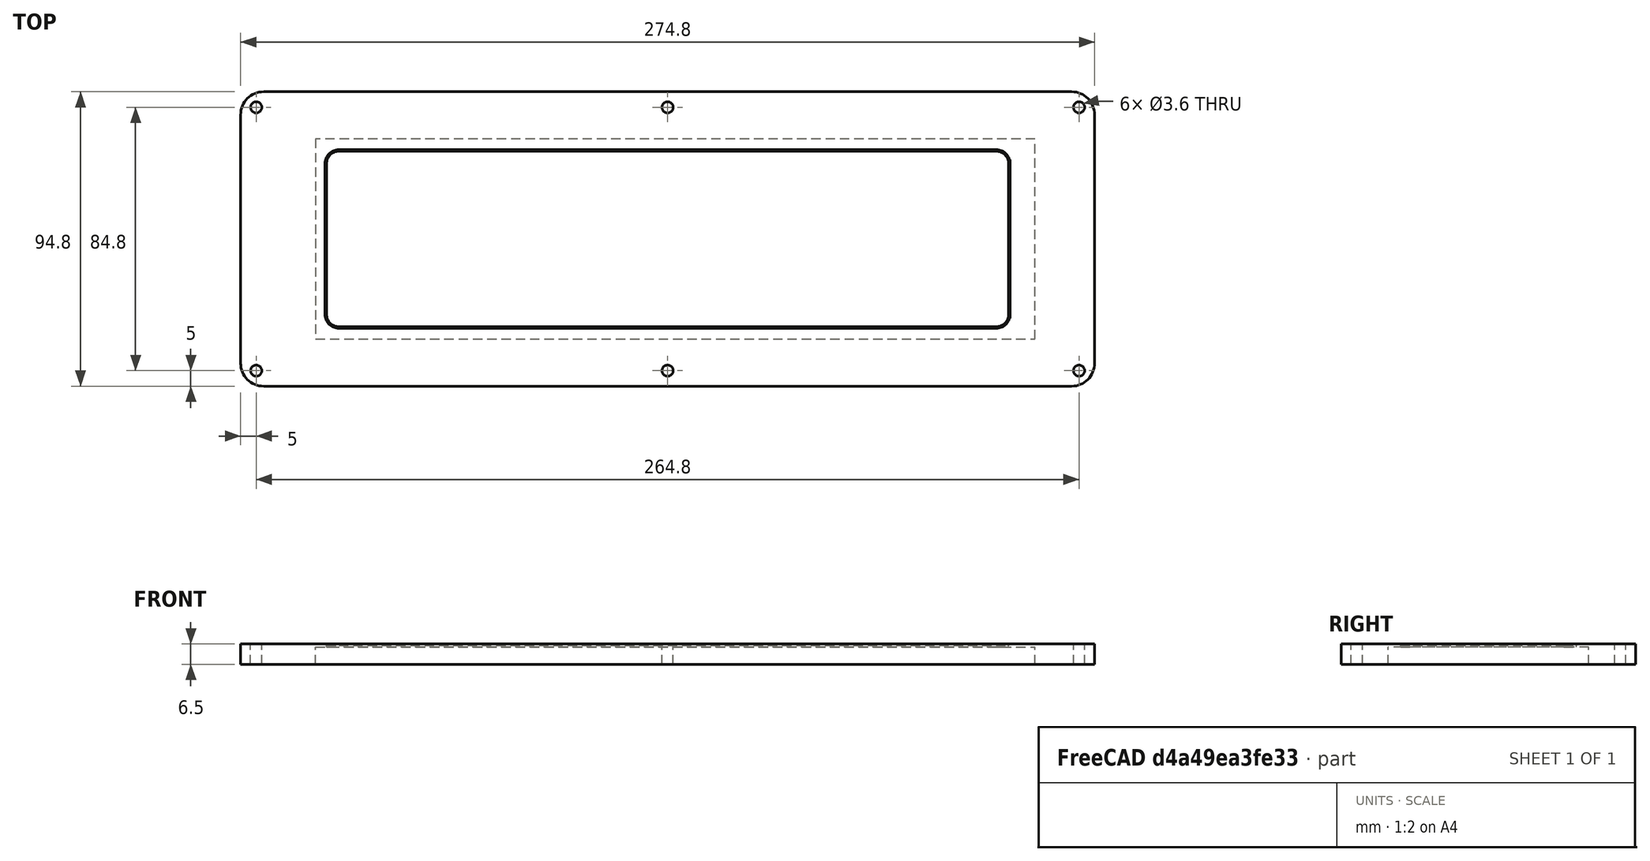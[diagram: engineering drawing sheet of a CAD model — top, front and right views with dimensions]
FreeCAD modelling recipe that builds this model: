
FCSTD DOCUMENT  (FreeCAD 1.0R39319 (Git))
Label: TopEnclosureDisplayFront
License: All rights reserved
LicenseURL: https://en.wikipedia.org/wiki/All_rights_reserved
objects: PartDesign::SubShapeBinder×5, PartDesign::Mirrored×3, App::Link×2, PartDesign::Pocket×2, PartDesign::Hole×2, PartDesign::Pad×1, PartDesign::MultiTransform×1, PartDesign::Chamfer×1, PartDesign::Body×1
note: 32 computed .brp shape members not serialized (recipe doc carries the construction recipe); baked Part::Feature solids carry a one-line shape summary decoded from their .brp
EXTERNAL_REF file=TopEnclosure.FCStd obj=Sketch
EXTERNAL_REF file=Spec.FCStd obj=Spreadsheet

FEATURE [App::Link] Link  label="MasterSketch"
  LinkedObject = -> <external TopEnclosure.FCStd>#Sketch
FEATURE [PartDesign::SubShapeBinder] Binder
  BindCopyOnChange = 0
  BindMode = 0
  ClaimChildren = false
  Context = -> Body [Binder.]
  Fuse = false
  MakeFace = true
  OffsetFill = false
  OffsetIntersection = false
  OffsetJoinType = 0
  OffsetOpenResult = false
  PartialLoad = false
  Refine = true
  Relative = true
  Support = -> [Link[Edge10,Edge9,Edge11,Edge12,Edge13,Edge14,Edge15,Edge16]]
  _Version = 2
FEATURE [PartDesign::SubShapeBinder] Binder001
  BindCopyOnChange = 0
  BindMode = 0
  ClaimChildren = false
  Context = -> Body [Binder001.]
  Fuse = false
  MakeFace = true
  OffsetFill = false
  OffsetIntersection = false
  OffsetJoinType = 0
  OffsetOpenResult = false
  PartialLoad = false
  Refine = true
  Relative = true
  Support = -> [Link[Edge39]]
  _Version = 2
FEATURE [PartDesign::SubShapeBinder] Binder002
  BindCopyOnChange = 0
  BindMode = 0
  ClaimChildren = false
  Context = -> Body [Binder002.]
  Fuse = false
  MakeFace = true
  OffsetFill = false
  OffsetIntersection = false
  OffsetJoinType = 0
  OffsetOpenResult = false
  PartialLoad = false
  Refine = true
  Relative = true
  Support = -> [Link[Edge40]]
  _Version = 2
FEATURE [PartDesign::SubShapeBinder] Binder004
  BindCopyOnChange = 0
  BindMode = 0
  ClaimChildren = false
  Context = -> Body [Binder004.]
  Fuse = false
  MakeFace = true
  OffsetFill = false
  OffsetIntersection = false
  OffsetJoinType = 0
  OffsetOpenResult = false
  PartialLoad = false
  Refine = true
  Relative = true
  Support = -> [Link[Edge35,Edge36,Edge33,Edge34]]
  _Version = 2
FEATURE [PartDesign::SubShapeBinder] Binder005
  BindCopyOnChange = 0
  BindMode = 0
  ClaimChildren = false
  Context = -> Body [Binder005.]
  Fuse = false
  MakeFace = true
  OffsetFill = false
  OffsetIntersection = false
  OffsetJoinType = 0
  OffsetOpenResult = false
  PartialLoad = false
  Refine = true
  Relative = true
  Support = -> [Link[Edge26,Edge25,Edge27,Edge32,Edge31,Edge28,Edge29,Edge30]]
  _Version = 2
FEATURE [App::Link] Link001  label="Vars"
  LinkedObject = -> <external Spec.FCStd>#Spreadsheet
FEATURE [PartDesign::Pad] Pad
  Direction = (0,0,1)
  Length = 6.5
  Length2 = 10
  Profile = -> Binder
  Refine = true
  Suppressed = false
  Type = 0
  expr: Length = <<Vars>>.display_depth + <<Vars>>.top_enclosure_front_depth
FEATURE [PartDesign::Pocket] Pocket
  BaseFeature = -> Pad
  Direction = (0,0,-1)
  Length = 5
  Length2 = 5
  Profile = -> Binder005
  Refine = true
  Reversed = true
  Suppressed = false
  Type = 1
FEATURE [PartDesign::Pocket] Pocket001
  BaseFeature = -> Pocket
  Direction = (0,0,-1)
  Length = 5.5
  Length2 = 5
  Profile = -> Binder004
  Refine = true
  Reversed = true
  Suppressed = false
  Type = 0
  expr: Length = <<Vars>>.display_depth
FEATURE [PartDesign::Hole] Hole
  BaseFeature = -> Pocket001
  CustomThreadClearance = 0
  Depth = 25
  DepthType = 0
  Diameter = 3.6
  DrillForDepth = false
  DrillPoint = 1
  DrillPointAngle = 118
  HoleCutCountersinkAngle = 90
  HoleCutCustomValues = false
  HoleCutDepth = 0
  HoleCutDiameter = 6.1
  HoleCutType = 0
  ModelThread = false
  Profile = -> Binder001
  Refine = true
  Reversed = true
  Suppressed = false
  Tapered = false
  TaperedAngle = 90
  ThreadClass = 0
  ThreadDepth = 25
  ThreadDepthType = 0
  ThreadDirection = 0
  ThreadFit = 2
  ThreadSize = 9
  ThreadType = 1
  Threaded = false
  UseCustomThreadClearance = false
FEATURE [PartDesign::Mirrored] Mirrored
  MirrorPlane = -> YZ_Plane
  Refine = true
  Suppressed = false
  TransformMode = 0
FEATURE [PartDesign::Mirrored] Mirrored001
  MirrorPlane = -> XZ_Plane
  Refine = true
  Suppressed = false
  TransformMode = 0
FEATURE [PartDesign::MultiTransform] MultiTransform
  BaseFeature = -> Hole
  Originals = -> [Hole]
  Refine = true
  Suppressed = false
  TransformMode = 0
  Transformations = -> [Mirrored,Mirrored001]
FEATURE [PartDesign::Hole] Hole001
  BaseFeature = -> MultiTransform
  CustomThreadClearance = 0
  Depth = 25
  DepthType = 0
  Diameter = 3.6
  DrillForDepth = false
  DrillPoint = 1
  DrillPointAngle = 118
  HoleCutCountersinkAngle = 90
  HoleCutCustomValues = false
  HoleCutDepth = 0
  HoleCutDiameter = 6.1
  HoleCutType = 0
  ModelThread = false
  Profile = -> Binder002
  Refine = true
  Reversed = true
  Suppressed = false
  Tapered = false
  TaperedAngle = 90
  ThreadClass = 0
  ThreadDepth = 25
  ThreadDepthType = 0
  ThreadDirection = 0
  ThreadFit = 2
  ThreadSize = 9
  ThreadType = 1
  Threaded = false
  UseCustomThreadClearance = false
FEATURE [PartDesign::Mirrored] Mirrored002
  BaseFeature = -> Hole001
  MirrorPlane = -> XZ_Plane
  Originals = -> [Hole001]
  Refine = true
  Suppressed = false
  TransformMode = 0
FEATURE [PartDesign::Chamfer] Chamfer
  Angle = 45
  Base = -> Mirrored002 [Edge39]
  BaseFeature = -> Mirrored002
  ChamferType = 0
  FlipDirection = false
  Refine = true
  Size = 0.5
  Size2 = 1
  SupportTransform = false
  Suppressed = false
  UseAllEdges = false
FEATURE [PartDesign::Body] Body  label="Top Enclosure Display Front"
  AllowCompound = false
  Group = -> [Binder,Binder001,Binder002,Binder004,Binder005,Pad,Pocket,Pocket001,Hole,MultiTransform,Mirrored,Mirrored001,Hole001,Mirrored002,Chamfer]
  Origin = -> Origin
  Tip = -> Chamfer

RESOLVED EXTERNAL PARTS (link-assembly join: the EXTERNAL_REF files above that resolve inside this repo's crawl, each included once):
---- part Spec.FCStd = doc fcstd_a8ec68f4a39c ----
FCSTD DOCUMENT  (FreeCAD 1.0R39319 (Git))
Label: Spec
License: All rights reserved
LicenseURL: https://en.wikipedia.org/wiki/All_rights_reserved
objects: Spreadsheet::Sheet×1

FEATURE [Spreadsheet::Sheet] Spreadsheet  label="Vars"
  cells = A1='Common; A2='clearance; B2(clearance)=0.2; A3='nut_inserts_m2; B3(nut_inserts_m2)=3.5; A4='nut_inserts_m3; B4(nut_inserts_m3)=4.5; A5='wall; B5(wall)=2.5; A6='ext_radius; B6(ext_radius)=10; A7='hood_angle; B7(hood_angle)=4; A12='Display; A13='display_width; B13(display_width)=231.3; A14='display_height; B14(display_height)=64.3; A15='display_depth; B15(display_depth)=5.5; A16='display_offset_bottom; B16(display_offset_bottom)==3 + display_view_offset; C16='display_view_offset; D16(display_view_offset)=1; A17='display_offset_left; B17(display_offset_left)==2.5 + display_view_offset; A18='display_offset_right; B18(display_offset_right)==7.5 + display_view_offset; A19='display_offset_top; B19(display_offset_top)==3 + display_view_offset; F20='b; A21='Top Enclosure; A22='top_enclosure_width; B22(top_enclosure_width)=280; A23='top_enclosure_height; B23(top_enclosure_height)=100; A24='top_enclosure_front_depth; B24(top_enclosure_front_depth)=1; A25='top_enclosure_back_depth; B25(top_enclosure_back_depth)==wall; A26='top_enclosure_display_back_depth; B26(top_enclosure_display_back_depth)=1; A27='top_enclosure_depth; B27(top_enclosure_depth)=14; A28='top_enclosure_internal_depth; B28(top_enclosure_internal_depth)==top_enclosure_depth - top_enclosure_front_depth - display_depth - top_enclosure_display_back_depth - top_enclosure_back_depth + wall; A30='Bottom Enclosure; A31='bottom_enclosure_width; B31(bottom_enclosure_width)==top_enclosure_width; A32='bottom_enclosure_height; B32(bottom_enclosure_height)=160; A33='bottom_enclosure_depth; B33(bottom_enclosure_depth)=30; A35='Keyboard Plate; A36='keyboard_plate_width; B36(keyboard_plate_width)==235 - 2; A37='keyboard_plate_height; B37(keyboard_plate_height)==82.5 - 2; A38='keyboard_plate_radius; B38(kayboard_plate_radius)==ext_radius / 2; A40='Keyboard Plate; A41='wire_hole_offset_x; B41(wire_hole_offset_x)=40; A42='wire_hole_width; B42(wire_hole_width)=30; A43='wire_hole_height; B43(wire_hole_height)=9
---- part TopEnclosure.FCStd = doc fcstd_a96d0c470227 ----
FCSTD DOCUMENT  (FreeCAD 1.0R39319 (Git))
Label: TopEnclosure
License: All rights reserved
LicenseURL: https://en.wikipedia.org/wiki/All_rights_reserved
objects: App::Link×1, Sketcher::SketchObject×1
note: 2 computed .brp shape members not serialized (recipe doc carries the construction recipe); baked Part::Feature solids carry a one-line shape summary decoded from their .brp
EXTERNAL_REF file=Spec.FCStd obj=Spreadsheet

FEATURE [App::Link] Link  label="Vars"
  LinkedObject = -> <external Spec.FCStd>#Spreadsheet
FEATURE [Sketcher::SketchObject] Sketch  label="MasterSketch"
  ArcFitTolerance = 1e-06
  FullyConstrained = true
  MakeInternals = false
  expr: Constraints[100] = <<Vars>>.display_offset_left
  expr: Constraints[101] = <<Vars>>.display_offset_right
  expr: Constraints[102] = <<Vars>>.display_offset_bottom
  expr: Constraints[150] = <<Vars>>.ext_radius
  expr: Constraints[64] = <<Vars>>.wall
  expr: Constraints[65] = <<Vars>>.top_enclosure_height
  expr: Constraints[66] = <<Vars>>.top_enclosure_width
  expr: Constraints[67] = <<Vars>>.clearance / 2
  expr: Constraints[96] = <<Vars>>.display_width + <<Vars>>.clearance
  expr: Constraints[97] = <<Vars>>.display_height + <<Vars>>.clearance
  expr: Constraints[99] = <<Vars>>.display_offset_top
  sketch-geometry (62):
    g0: LineSegment StartX=-137.5 StartY=40 StartZ=0 EndX=-137.5 EndY=-40 EndZ=0
    g1: LineSegment StartX=-130 StartY=-47.5 StartZ=0 EndX=130 EndY=-47.5 EndZ=0
    g2: LineSegment StartX=137.5 StartY=-40 StartZ=0 EndX=137.5 EndY=40 EndZ=0
    g3: LineSegment StartX=130 StartY=47.5 StartZ=0 EndX=-130 EndY=47.5 EndZ=0
    g4: ArcOfCircle CenterX=-130 CenterY=40 CenterZ=0 NormalX=0 NormalY=0 NormalZ=1 AngleXU=0 Radius=7.5 StartAngle=1.5708 EndAngle=3.14159
    g5: ArcOfCircle CenterX=-130 CenterY=-40 CenterZ=0 NormalX=0 NormalY=0 NormalZ=1 AngleXU=0 Radius=7.5 StartAngle=3.14159 EndAngle=4.71239
    g6: ArcOfCircle CenterX=130 CenterY=-40 CenterZ=0 NormalX=0 NormalY=0 NormalZ=1 AngleXU=0 Radius=7.5 StartAngle=4.71239 EndAngle=6.28319
    g7: ArcOfCircle CenterX=130 CenterY=40 CenterZ=0 NormalX=0 NormalY=0 NormalZ=1 AngleXU=0 Radius=7.5 StartAngle=4e-16 EndAngle=1.5708
    g8: GeomPoint [constr] X=-137.5 Y=47.5 Z=0
    g9: GeomPoint [constr] X=137.5 Y=-47.5 Z=0
    g10: LineSegment StartX=-137.4 StartY=40 StartZ=0 EndX=-137.4 EndY=-40 EndZ=0
    g11: LineSegment StartX=-130 StartY=-47.4 StartZ=0 EndX=130 EndY=-47.4 EndZ=0
    g12: LineSegment StartX=137.4 StartY=-40 StartZ=0 EndX=137.4 EndY=40 EndZ=0
    g13: LineSegment StartX=130 StartY=47.4 StartZ=0 EndX=-130 EndY=47.4 EndZ=0
    g14: ArcOfCircle CenterX=-130 CenterY=40 CenterZ=0 NormalX=0 NormalY=0 NormalZ=1 AngleXU=0 Radius=7.4 StartAngle=1.5708 EndAngle=3.14159
    g15: ArcOfCircle CenterX=-130 CenterY=-40 CenterZ=0 NormalX=0 NormalY=0 NormalZ=1 AngleXU=0 Radius=7.4 StartAngle=3.14159 EndAngle=4.71239
    g16: ArcOfCircle CenterX=130 CenterY=-40 CenterZ=0 NormalX=0 NormalY=0 NormalZ=1 AngleXU=0 Radius=7.4 StartAngle=4.71239 EndAngle=6.28319
    g17: ArcOfCircle CenterX=130 CenterY=40 CenterZ=0 NormalX=0 NormalY=0 NormalZ=1 AngleXU=0 Radius=7.4 StartAngle=3e-16 EndAngle=1.5708
    g18: GeomPoint [constr] X=-137.4 Y=47.4 Z=0
    g19: GeomPoint [constr] X=137.4 Y=-47.4 Z=0
    g20: LineSegment StartX=-140 StartY=40 StartZ=0 EndX=-140 EndY=-40 EndZ=0
    g21: LineSegment StartX=-130 StartY=-50 StartZ=0 EndX=130 EndY=-50 EndZ=0
    g22: LineSegment StartX=140 StartY=-40 StartZ=0 EndX=140 EndY=40 EndZ=0
    g23: LineSegment StartX=130 StartY=50 StartZ=0 EndX=-130 EndY=50 EndZ=0
    g24: ArcOfCircle CenterX=-130 CenterY=40 CenterZ=0 NormalX=0 NormalY=0 NormalZ=1 AngleXU=0 Radius=10 StartAngle=1.5708 EndAngle=3.14159
    g25: ArcOfCircle CenterX=-130 CenterY=-40 CenterZ=0 NormalX=0 NormalY=0 NormalZ=1 AngleXU=0 Radius=10 StartAngle=3.14159 EndAngle=4.71239
    g26: ArcOfCircle CenterX=130 CenterY=-40 CenterZ=0 NormalX=0 NormalY=0 NormalZ=1 AngleXU=0 Radius=10 StartAngle=4.71239 EndAngle=6.28319
    g27: ArcOfCircle CenterX=130 CenterY=40 CenterZ=0 NormalX=0 NormalY=0 NormalZ=1 AngleXU=0 Radius=10 StartAngle=0 EndAngle=1.5708
    g28: GeomPoint [constr] X=-140 Y=50 Z=0
    g29: GeomPoint [constr] X=140 Y=-50 Z=0
    g30: LineSegment StartX=-109.75 StartY=24.25 StartZ=0 EndX=-109.75 EndY=-24.25 EndZ=0
    g31: LineSegment StartX=-105.75 StartY=-28.25 StartZ=0 EndX=105.75 EndY=-28.25 EndZ=0
    g32: LineSegment StartX=109.75 StartY=-24.25 StartZ=0 EndX=109.75 EndY=24.25 EndZ=0
    g33: LineSegment StartX=105.75 StartY=28.25 StartZ=0 EndX=-105.75 EndY=28.25 EndZ=0
    g34: ArcOfCircle CenterX=-105.75 CenterY=24.25 CenterZ=0 NormalX=0 NormalY=0 NormalZ=1 AngleXU=0 Radius=4 StartAngle=1.5708 EndAngle=3.14159
    g35: ArcOfCircle CenterX=-105.75 CenterY=-24.25 CenterZ=0 NormalX=0 NormalY=0 NormalZ=1 AngleXU=0 Radius=4 StartAngle=3.14159 EndAngle=4.71239
    g36: ArcOfCircle CenterX=105.75 CenterY=-24.25 CenterZ=0 NormalX=0 NormalY=0 NormalZ=1 AngleXU=0 Radius=4 StartAngle=4.71239 EndAngle=6.28319
    g37: ArcOfCircle CenterX=105.75 CenterY=24.25 CenterZ=0 NormalX=0 NormalY=0 NormalZ=1 AngleXU=0 Radius=4 StartAngle=0 EndAngle=1.5708
    g38: GeomPoint [constr] X=-109.75 Y=28.25 Z=0
    g39: GeomPoint [constr] X=109.75 Y=-28.25 Z=0
    g40: LineSegment StartX=-113.25 StartY=32.25 StartZ=0 EndX=-113.25 EndY=-32.25 EndZ=0
    g41: LineSegment StartX=-113.25 StartY=-32.25 StartZ=0 EndX=118.25 EndY=-32.25 EndZ=0
    g42: LineSegment StartX=118.25 StartY=-32.25 StartZ=0 EndX=118.25 EndY=32.25 EndZ=0
    g43: LineSegment StartX=118.25 StartY=32.25 StartZ=0 EndX=-113.25 EndY=32.25 EndZ=0
    g44: Circle CenterX=-137.703 CenterY=47.7033 CenterZ=0 NormalX=0 NormalY=0 NormalZ=1 AngleXU=0 Radius=12.5
    g45: Circle CenterX=0 CenterY=49.9 CenterZ=0 NormalX=0 NormalY=0 NormalZ=1 AngleXU=0 Radius=12.5
    g46: Circle CenterX=-132.4 CenterY=42.4 CenterZ=0 NormalX=0 NormalY=0 NormalZ=1 AngleXU=0 Radius=1.5
    g47: Circle CenterX=0 CenterY=42.4 CenterZ=0 NormalX=0 NormalY=0 NormalZ=1 AngleXU=0 Radius=1.5
    g48: LineSegment [constr] StartX=0 StartY=42.4 StartZ=0 EndX=0 EndY=37.4 EndZ=0
    g49: LineSegment [constr] StartX=-132.4 StartY=42.4 StartZ=0 EndX=-128.864 EndY=38.8645 EndZ=0
    g50: LineSegment [constr] StartX=-132.4 StartY=42.4 StartZ=0 EndX=-137.703 EndY=47.7033 EndZ=0
    g51: LineSegment StartX=121.25 StartY=26.25 StartZ=0 EndX=121.25 EndY=25.25 EndZ=0
    g52: LineSegment StartX=122.25 StartY=24.25 StartZ=0 EndX=130.25 EndY=24.25 EndZ=0
    g53: LineSegment StartX=131.25 StartY=25.25 StartZ=0 EndX=131.25 EndY=26.25 EndZ=0
    g54: LineSegment StartX=130.25 StartY=27.25 StartZ=0 EndX=122.25 EndY=27.25 EndZ=0
    g55: ArcOfCircle CenterX=122.25 CenterY=26.25 CenterZ=0 NormalX=0 NormalY=0 NormalZ=1 AngleXU=0 Radius=1 StartAngle=1.5708 EndAngle=3.14159
    g56: ArcOfCircle CenterX=122.25 CenterY=25.25 CenterZ=0 NormalX=0 NormalY=0 NormalZ=1 AngleXU=0 Radius=1 StartAngle=3.14159 EndAngle=4.71239
    g57: ArcOfCircle CenterX=130.25 CenterY=25.25 CenterZ=0 NormalX=0 NormalY=0 NormalZ=1 AngleXU=0 Radius=1 StartAngle=4.71239 EndAngle=6.28319
    g58: ArcOfCircle CenterX=130.25 CenterY=26.25 CenterZ=0 NormalX=0 NormalY=0 NormalZ=1 AngleXU=0 Radius=1 StartAngle=1e-16 EndAngle=1.5708
    g59: GeomPoint [constr] X=121.25 Y=27.25 Z=0
    g60: GeomPoint [constr] X=131.25 Y=24.25 Z=0
    g61: LineSegment [constr] StartX=126.25 StartY=32.25 StartZ=0 EndX=126.25 EndY=-32.25 EndZ=0
  constraints (151):
    c: Tangent(g0,g4) = -1.5708
    c: Tangent(g0,g5) = -1.5708
    c: Tangent(g1,g5) = -1.5708
    c: Tangent(g1,g6) = -1.5708
    c: Tangent(g2,g6) = -1.5708
    c: Tangent(g2,g7) = -1.5708
    c: Tangent(g3,g7) = -1.5708
    c: Tangent(g3,g4) = -1.5708
    c: Vertical(g0)
    c: Vertical(g2)
    c: Horizontal(g1)
    c: Horizontal(g3)
    c: Equal(g4,g5)
    c: Equal(g5,g6)
    c: Equal(g6,g7)
    c: PointOnObject(g8,g0)
    c: PointOnObject(g8,g3)
    c: PointOnObject(g9,g1)
    c: PointOnObject(g9,g2)
    c: Tangent(g10,g14) = -1.5708
    c: Tangent(g10,g15) = -1.5708
    c: Tangent(g11,g15) = -1.5708
    c: Tangent(g11,g16) = -1.5708
    c: Tangent(g12,g16) = -1.5708
    c: Tangent(g12,g17) = -1.5708
    c: Tangent(g13,g17) = -1.5708
    c: Tangent(g13,g14) = -1.5708
    c: Vertical(g10)
    c: Vertical(g12)
    c: Horizontal(g11)
    c: Horizontal(g13)
    c: Equal(g14,g15)
    c: Equal(g15,g16)
    c: Equal(g16,g17)
    c: PointOnObject(g18,g10)
    c: PointOnObject(g18,g13)
    c: PointOnObject(g19,g11)
    c: PointOnObject(g19,g12)
    c: Tangent(g20,g24) = -1.5708
    c: Tangent(g20,g25) = -1.5708
    c: Tangent(g21,g25) = -1.5708
    c: Tangent(g21,g26) = -1.5708
    c: Tangent(g22,g26) = -1.5708
    c: Tangent(g22,g27) = -1.5708
    c: Tangent(g23,g27) = -1.5708
    c: Tangent(g23,g24) = -1.5708
    c: Vertical(g20)
    c: Vertical(g22)
    c: Horizontal(g21)
    c: Horizontal(g23)
    c: Equal(g24,g25)
    c: Equal(g25,g26)
    c: Equal(g26,g27)
    c: PointOnObject(g28,g20)
    c: PointOnObject(g28,g23)
    c: PointOnObject(g29,g21)
    c: PointOnObject(g29,g22)
    c: Symmetric(g25,g27,g-1)
    c: Symmetric(g5,g7,g-1)
    c: Symmetric(g15,g17,g-1)
    c: Horizontal(g20,g0)
    c: Horizontal(g0,g10)
    c: Vertical(g13,g3)
    c: Vertical(g3,g23)
    c: DistanceX(g20,g0) = 2.5
    c: DistanceY(g21,g23) = 100
    c: DistanceX(g20,g22) = 280
    c: DistanceY(g13,g3) = 0.1
    c: Tangent(g30,g34) = -1.5708
    c: Tangent(g30,g35) = -1.5708
    c: Tangent(g31,g35) = -1.5708
    c: Tangent(g31,g36) = -1.5708
    c: Tangent(g32,g36) = -1.5708
    c: Tangent(g32,g37) = -1.5708
    c: Tangent(g33,g37) = -1.5708
    c: Tangent(g33,g34) = -1.5708
    c: Vertical(g30)
    c: Vertical(g32)
    c: Horizontal(g31)
    c: Horizontal(g33)
    c: Equal(g34,g35)
    c: Equal(g35,g36)
    c: Equal(g36,g37)
    c: PointOnObject(g38,g30)
    c: PointOnObject(g38,g33)
    c: PointOnObject(g39,g31)
    c: PointOnObject(g39,g32)
    c: Coincident(g40,g41)
    c: Coincident(g41,g42)
    c: Coincident(g42,g43)
    c: Coincident(g43,g40)
    c: Vertical(g40)
    c: Vertical(g42)
    c: Horizontal(g41)
    c: Horizontal(g43)
    c: Symmetric(g35,g37,g-1)
    c: DistanceX(g41,g41) = 231.5
    c: DistanceY(g42,g42) = 64.5
    c: Radius(g34) = 4
    c: DistanceY(g33,g40) = 4
    c: DistanceX(g40,g30) = 3.5
    c: DistanceX(g32,g42) = 8.5
    c: DistanceY(g41,g31) = 4
    c: PointOnObject(g45,g-2)
    c: PointOnObject(g47,g-2)
    c: Equal(g46,g47)
    c: Equal(g45,g44)
    c: Diameter(g45) = 25
    c: Coincident(g48,g47)
    c: PointOnObject(g48,g45)
    c: Vertical(g48)
    c: DistanceY(g48,g48) = 5
    c: Horizontal(g47,g46)
    c: Coincident(g49,g46)
    c: PointOnObject(g49,g44)
    c: Equal(g49,g48)
    c: PointOnObject(g4,g49)
    c: Coincident(g50,g46)
    c: Coincident(g50,g44)
    c: Parallel(g49,g50)
    c: PointOnObject(g28,g50)
    c: DistanceY(g46,g13) = 5
    c: Diameter(g46) = 3
    c: Tangent(g51,g55) = -1.5708
    c: Tangent(g51,g56) = -1.5708
    c: Tangent(g52,g56) = -1.5708
    c: Tangent(g52,g57) = -1.5708
    c: Tangent(g53,g57) = -1.5708
    c: Tangent(g53,g58) = -1.5708
    c: Tangent(g54,g58) = -1.5708
    c: Tangent(g54,g55) = -1.5708
    c: Vertical(g51)
    c: Vertical(g53)
    c: Horizontal(g52)
    c: Horizontal(g54)
    c: Equal(g55,g56)
    c: Equal(g56,g57)
    c: Equal(g57,g58)
    c: PointOnObject(g59,g51)
    c: PointOnObject(g59,g54)
    c: PointOnObject(g60,g52)
    c: PointOnObject(g60,g53)
    c: Radius(g56) = 1
    c: DistanceY(g52,g54) = 3
    c: DistanceX(g51,g53) = 10
    c: Equal(g42,g61)
    c: Horizontal(g42,g61)
    c: DistanceX(g42,g61) = 8
    c: Symmetric(g54,g54,g61)
    c: DistanceY(g54,g42) = 5
    c: Radius(g25) = 10
